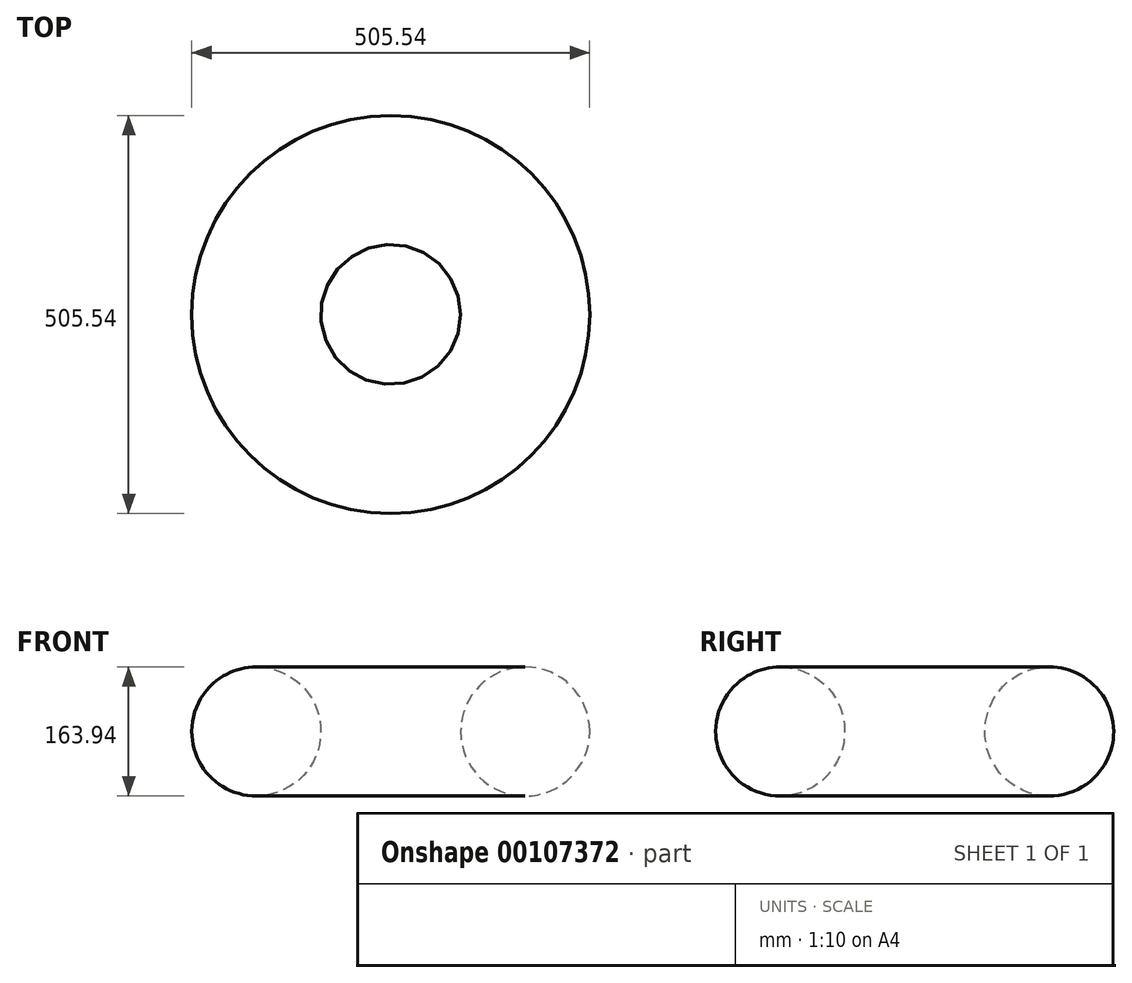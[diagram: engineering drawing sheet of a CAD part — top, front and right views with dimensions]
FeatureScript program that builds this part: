
annotation { "Feature Type Name" : "Feature", "Feature Type Description" : "" }
export const myFeature = defineFeature(function(context is Context, id is Id, definition is map)
    precondition{}
    {
        {
            var Q0;
            Q0=qCreatedBy(makeId("Front.planeOp"),FACE);
            var sketch = newSketch(context, id + "F0", { "sketchPlane" : qUnion([Q0])});
            skPoint(sketch, "E0", {"position": v(170.8, 0) * mm});
            skCircle(sketch, "E1", {"center": v(170.8, 0) * mm, "radius": 81.97 * mm});
            skSolve(sketch);
        }
        {
            var Q0;
            Q0=qCreatedBy(makeId("Front.planeOp"),FACE);
            var sketch = newSketch(context, id + "F1", { "sketchPlane" : qUnion([Q0])});
            skLineSegment(sketch, "E2", {"start": v(0, 0) * mm, "end": v(0, -188.1) * mm});
            skSolve(sketch);
        }
        {
            var Q0;
            Q0=makeQuery(id+"F0.imprint","IMPRINT",FACE,{"disambiguationData":[TD([[makeQuery(id+"F0.imprint","IMPRINT",EDGE,{"derivedFrom":sQuery(id+"F0.wireOp",EDGE,"E1")}),1.0]])]});
            var Q1;
            Q1=sQuery(id+"F1.wireOp",EDGE,"E2");
            revolve(context, id + "F2", {"entities" : qUnion([Q0]), "axis" : qUnion([Q1]), "revolveType" : RevolveType.FULL});
        }
    });
